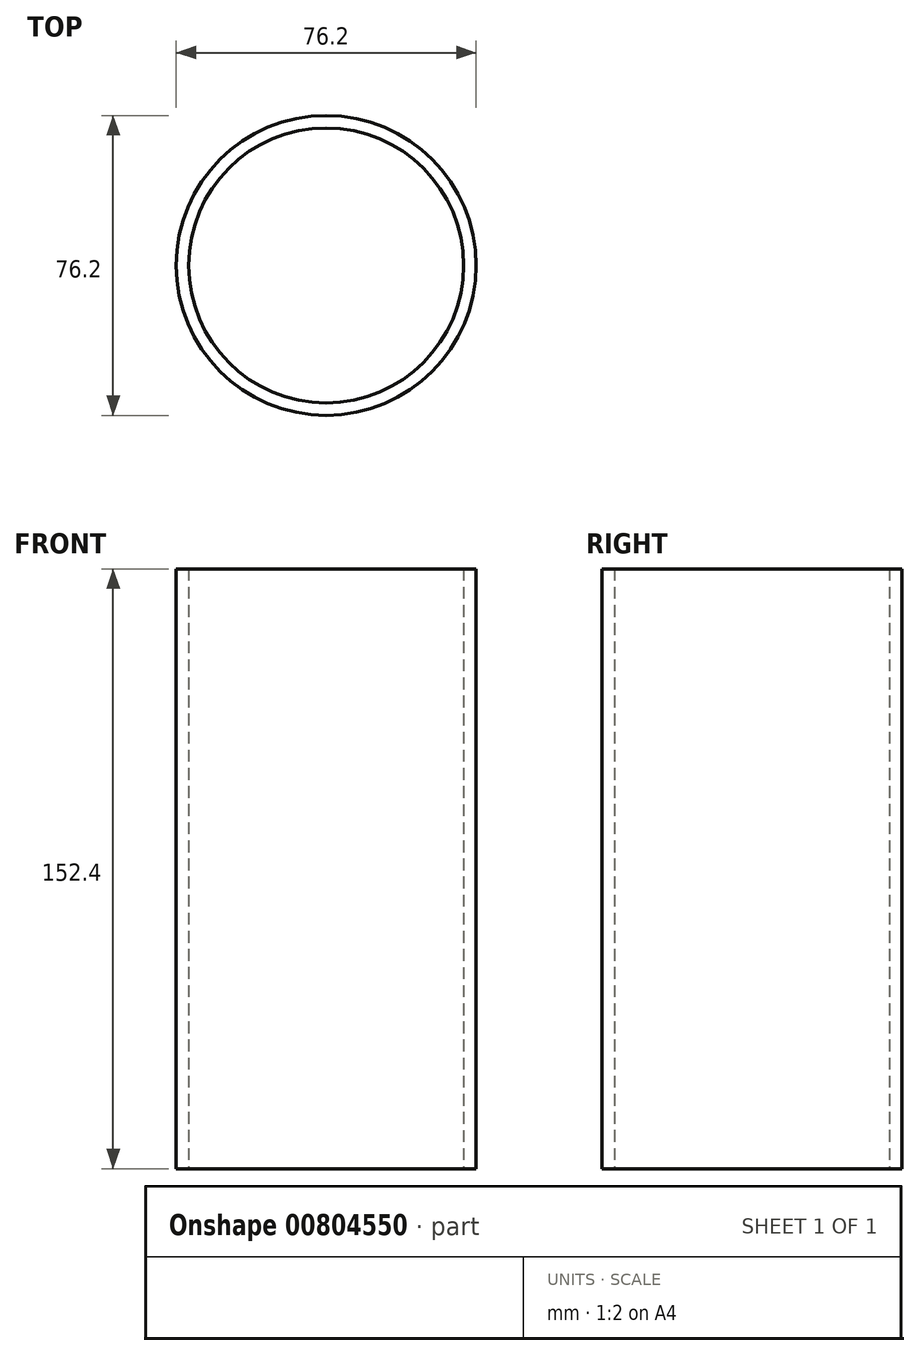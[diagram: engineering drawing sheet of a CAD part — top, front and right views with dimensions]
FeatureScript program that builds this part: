
annotation { "Feature Type Name" : "Feature", "Feature Type Description" : "" }
export const myFeature = defineFeature(function(context is Context, id is Id, definition is map)
    precondition{}
    {
        {
            var Q0;
            Q0=qCreatedBy(makeId("Top.planeOp"),FACE);
            var sketch = newSketch(context, id + "F0", { "sketchPlane" : qUnion([Q0])});
            skCircle(sketch, "E0", {"center": v(0, 0) * mm, "radius": 38.1 * mm});
            skCircle(sketch, "E1", {"center": v(0, 0) * mm, "radius": 34.93 * mm});
            skSolve(sketch);
        }
        {
            var Q0;
            Q0=qSketchRegion(id+"F0",true);
            extrude(context, id + "F1", {"entities" : qUnion([Q0]), "depth" : 152.4 * mm});
        }
    });
